# Revit family: OASIS SH-3232 ABF
name_source: partatom
category: Plumbing Fixtures
revit_build: Autodesk Revit 2017 (Build: 20161006_0315(x64)
units: mm (PartAtom-declared; Revit-internal decimal feet)

## family parameters
Always vertical = Yes
Cut with Voids When Loaded = No
OmniClass Number = 23.45.05.14.21.11
OmniClass Title = Bath/Shower Units
Part Type = Normal
Room Calculation Point = No
Round Connector Dimension = Use Diameter
Shared = No
Work Plane-Based = No

## types (1)
- Base Model, 3SF, 3SM, FH, FHV packages
    BIM Model By = www.epoch-design.com
    Cold Water Connector = Cold Water Connection
    Color = <By Category>
    Grab Bar Finish = <By Category>
    Hot Water Connector = Hot Water Connection
    Manufacturer = OASIS
    Model = SH-3232 ABF
    Sanitary Connector = Sanitary Connection
    Sanitary Radius = 1 11/16"
    Seat Finish = <By Category>
    Shower Rod = No
    Stainless steel = <By Category>
    Type Comments = Shower
    URL = www.oasisbath.com

## geometry (parser evidence)
native form markers: Sweep x6
no freeform markers — native parametric forms only
